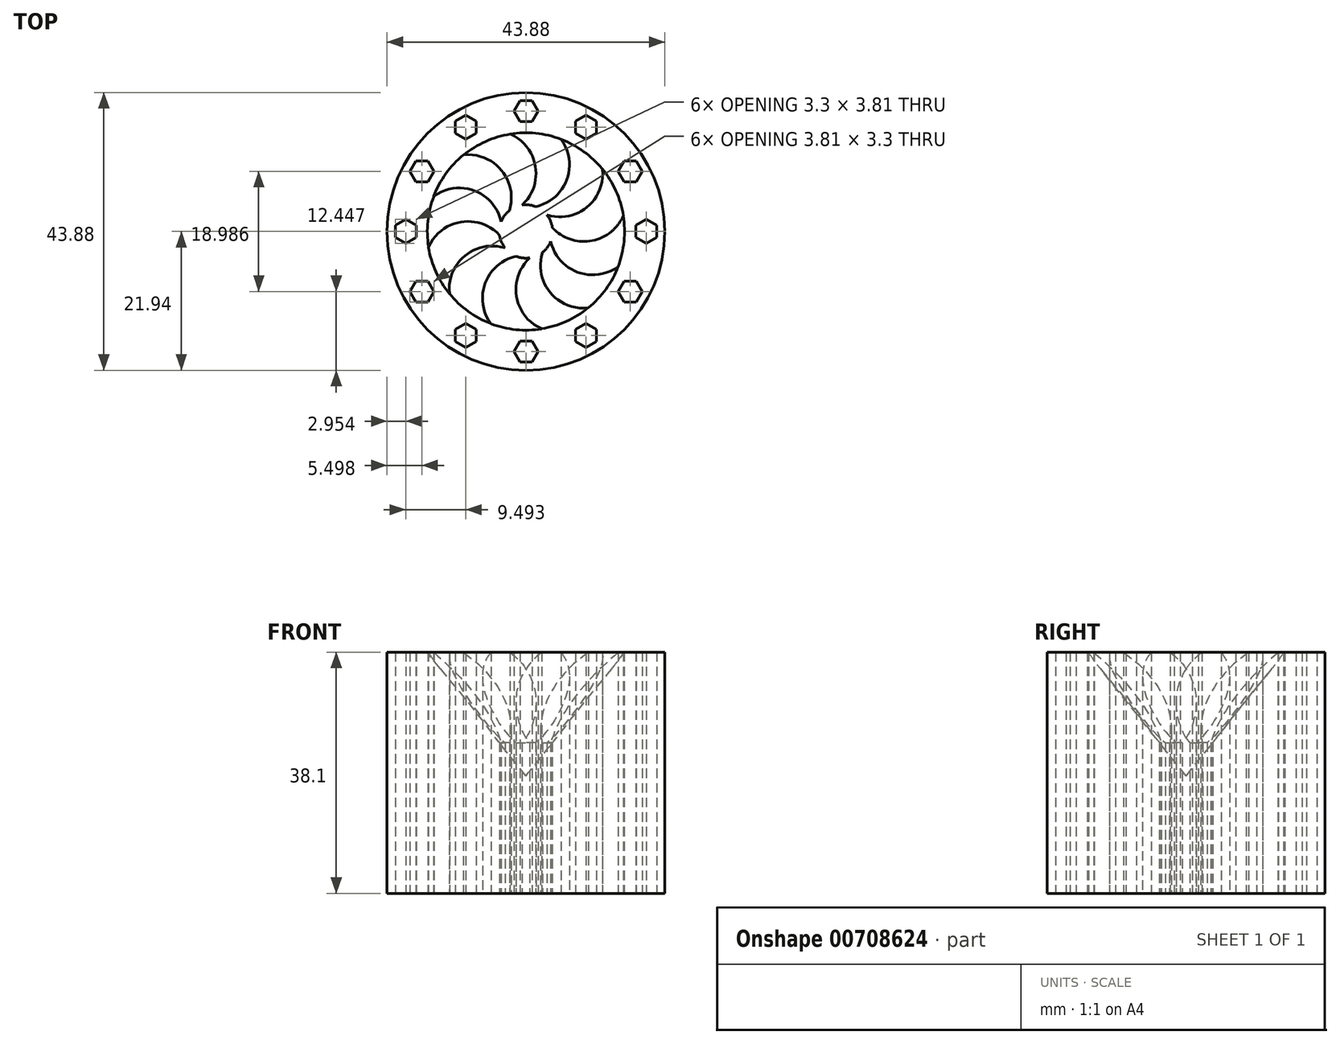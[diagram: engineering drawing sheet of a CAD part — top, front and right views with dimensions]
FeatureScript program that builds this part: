
annotation { "Feature Type Name" : "Feature", "Feature Type Description" : "" }
export const myFeature = defineFeature(function(context is Context, id is Id, definition is map)
    precondition{}
    {
        {
            var Q0;
            Q0=qCreatedBy(makeId("Top.planeOp"),FACE);
            var sketch = newSketch(context, id + "F0", { "sketchPlane" : qUnion([Q0])});
            skCircle(sketch, "E0", {"center": v(0, 0) * mm, "radius": 21.94 * mm});
            skCircle(sketch, "E1.0", {"center": v(0, 0) * mm, "radius": 15.59 * mm});
            skCircle(sketch, "E2.cCircle", {"center": v(0, 18.99) * mm, "radius": 1.65 * mm, "construction": true});
            skLineSegment(sketch, "E2.0", {"start": v(0.95, 17.34) * mm, "end": v(-0.95, 17.34) * mm});
            skLineSegment(sketch, "E2.1", {"start": v(-0.95, 17.34) * mm, "end": v(-1.9, 18.99) * mm});
            skLineSegment(sketch, "E2.2", {"start": v(-1.9, 18.99) * mm, "end": v(-0.95, 20.64) * mm});
            skLineSegment(sketch, "E2.3", {"start": v(-0.95, 20.64) * mm, "end": v(0.95, 20.64) * mm});
            skLineSegment(sketch, "E2.4", {"start": v(0.95, 20.64) * mm, "end": v(1.9, 18.99) * mm});
            skLineSegment(sketch, "E2.5", {"start": v(1.9, 18.99) * mm, "end": v(0.95, 17.34) * mm});
            skPoint(sketch, "E2.0.midPoint", {"position": v(0, 17.34) * mm});
            skLineSegment(sketch, "E3.1.0", {"start": v(-11.14, 15.5) * mm, "end": v(-11.14, 17.4) * mm});
            skLineSegment(sketch, "E3.1.1", {"start": v(-11.14, 17.4) * mm, "end": v(-9.5, 18.35) * mm});
            skLineSegment(sketch, "E3.1.2", {"start": v(-9.5, 18.35) * mm, "end": v(-7.84, 17.4) * mm});
            skLineSegment(sketch, "E3.1.3", {"start": v(-7.84, 17.4) * mm, "end": v(-7.84, 15.5) * mm});
            skLineSegment(sketch, "E3.1.4", {"start": v(-7.84, 15.5) * mm, "end": v(-9.5, 14.54) * mm});
            skLineSegment(sketch, "E3.1.5", {"start": v(-9.5, 14.54) * mm, "end": v(-11.14, 15.5) * mm});
            skLineSegment(sketch, "E3.2.0", {"start": v(-17.4, 7.84) * mm, "end": v(-18.35, 9.5) * mm});
            skLineSegment(sketch, "E3.2.1", {"start": v(-18.35, 9.5) * mm, "end": v(-17.4, 11.14) * mm});
            skLineSegment(sketch, "E3.2.2", {"start": v(-17.4, 11.14) * mm, "end": v(-15.5, 11.14) * mm});
            skLineSegment(sketch, "E3.2.3", {"start": v(-15.5, 11.14) * mm, "end": v(-14.54, 9.5) * mm});
            skLineSegment(sketch, "E3.2.4", {"start": v(-14.54, 9.5) * mm, "end": v(-15.5, 7.84) * mm});
            skLineSegment(sketch, "E3.2.5", {"start": v(-15.5, 7.84) * mm, "end": v(-17.4, 7.84) * mm});
            skLineSegment(sketch, "E3.3.0", {"start": v(-18.99, -1.9) * mm, "end": v(-20.64, -0.95) * mm});
            skLineSegment(sketch, "E3.3.1", {"start": v(-20.64, -0.95) * mm, "end": v(-20.64, 0.95) * mm});
            skLineSegment(sketch, "E3.3.2", {"start": v(-20.64, 0.95) * mm, "end": v(-18.99, 1.9) * mm});
            skLineSegment(sketch, "E3.3.3", {"start": v(-18.99, 1.9) * mm, "end": v(-17.34, 0.95) * mm});
            skLineSegment(sketch, "E3.3.4", {"start": v(-17.34, 0.95) * mm, "end": v(-17.34, -0.95) * mm});
            skLineSegment(sketch, "E3.3.5", {"start": v(-17.34, -0.95) * mm, "end": v(-18.99, -1.9) * mm});
            skLineSegment(sketch, "E3.4.0", {"start": v(-15.5, -11.14) * mm, "end": v(-17.4, -11.14) * mm});
            skLineSegment(sketch, "E3.4.1", {"start": v(-17.4, -11.14) * mm, "end": v(-18.35, -9.5) * mm});
            skLineSegment(sketch, "E3.4.2", {"start": v(-18.35, -9.5) * mm, "end": v(-17.4, -7.84) * mm});
            skLineSegment(sketch, "E3.4.3", {"start": v(-17.4, -7.84) * mm, "end": v(-15.5, -7.84) * mm});
            skLineSegment(sketch, "E3.4.4", {"start": v(-15.5, -7.84) * mm, "end": v(-14.54, -9.5) * mm});
            skLineSegment(sketch, "E3.4.5", {"start": v(-14.54, -9.5) * mm, "end": v(-15.5, -11.14) * mm});
            skLineSegment(sketch, "E3.5.0", {"start": v(-7.84, -17.4) * mm, "end": v(-9.5, -18.35) * mm});
            skLineSegment(sketch, "E3.5.1", {"start": v(-9.5, -18.35) * mm, "end": v(-11.14, -17.4) * mm});
            skLineSegment(sketch, "E3.5.2", {"start": v(-11.14, -17.4) * mm, "end": v(-11.14, -15.5) * mm});
            skLineSegment(sketch, "E3.5.3", {"start": v(-11.14, -15.5) * mm, "end": v(-9.5, -14.54) * mm});
            skLineSegment(sketch, "E3.5.4", {"start": v(-9.5, -14.54) * mm, "end": v(-7.84, -15.5) * mm});
            skLineSegment(sketch, "E3.5.5", {"start": v(-7.84, -15.5) * mm, "end": v(-7.84, -17.4) * mm});
            skLineSegment(sketch, "E3.6.0", {"start": v(1.9, -18.99) * mm, "end": v(0.95, -20.64) * mm});
            skLineSegment(sketch, "E3.6.1", {"start": v(0.95, -20.64) * mm, "end": v(-0.95, -20.64) * mm});
            skLineSegment(sketch, "E3.6.2", {"start": v(-0.95, -20.64) * mm, "end": v(-1.9, -18.99) * mm});
            skLineSegment(sketch, "E3.6.3", {"start": v(-1.9, -18.99) * mm, "end": v(-0.95, -17.34) * mm});
            skLineSegment(sketch, "E3.6.4", {"start": v(-0.95, -17.34) * mm, "end": v(0.95, -17.34) * mm});
            skLineSegment(sketch, "E3.6.5", {"start": v(0.95, -17.34) * mm, "end": v(1.9, -18.99) * mm});
            skLineSegment(sketch, "E3.7.0", {"start": v(11.14, -15.5) * mm, "end": v(11.14, -17.4) * mm});
            skLineSegment(sketch, "E3.7.1", {"start": v(11.14, -17.4) * mm, "end": v(9.5, -18.35) * mm});
            skLineSegment(sketch, "E3.7.2", {"start": v(9.5, -18.35) * mm, "end": v(7.84, -17.4) * mm});
            skLineSegment(sketch, "E3.7.3", {"start": v(7.84, -17.4) * mm, "end": v(7.84, -15.5) * mm});
            skLineSegment(sketch, "E3.7.4", {"start": v(7.84, -15.5) * mm, "end": v(9.5, -14.54) * mm});
            skLineSegment(sketch, "E3.7.5", {"start": v(9.5, -14.54) * mm, "end": v(11.14, -15.5) * mm});
            skLineSegment(sketch, "E3.8.0", {"start": v(17.4, -7.84) * mm, "end": v(18.35, -9.5) * mm});
            skLineSegment(sketch, "E3.8.1", {"start": v(18.35, -9.5) * mm, "end": v(17.4, -11.14) * mm});
            skLineSegment(sketch, "E3.8.2", {"start": v(17.4, -11.14) * mm, "end": v(15.5, -11.14) * mm});
            skLineSegment(sketch, "E3.8.3", {"start": v(15.5, -11.14) * mm, "end": v(14.54, -9.5) * mm});
            skLineSegment(sketch, "E3.8.4", {"start": v(14.54, -9.5) * mm, "end": v(15.5, -7.84) * mm});
            skLineSegment(sketch, "E3.8.5", {"start": v(15.5, -7.84) * mm, "end": v(17.4, -7.84) * mm});
            skLineSegment(sketch, "E3.9.0", {"start": v(18.99, 1.9) * mm, "end": v(20.64, 0.95) * mm});
            skLineSegment(sketch, "E3.9.1", {"start": v(20.64, 0.95) * mm, "end": v(20.64, -0.95) * mm});
            skLineSegment(sketch, "E3.9.2", {"start": v(20.64, -0.95) * mm, "end": v(18.99, -1.9) * mm});
            skLineSegment(sketch, "E3.9.3", {"start": v(18.99, -1.9) * mm, "end": v(17.34, -0.95) * mm});
            skLineSegment(sketch, "E3.9.4", {"start": v(17.34, -0.95) * mm, "end": v(17.34, 0.95) * mm});
            skLineSegment(sketch, "E3.9.5", {"start": v(17.34, 0.95) * mm, "end": v(18.99, 1.9) * mm});
            skLineSegment(sketch, "E3.10.0", {"start": v(15.5, 11.14) * mm, "end": v(17.4, 11.14) * mm});
            skLineSegment(sketch, "E3.10.1", {"start": v(17.4, 11.14) * mm, "end": v(18.35, 9.5) * mm});
            skLineSegment(sketch, "E3.10.2", {"start": v(18.35, 9.5) * mm, "end": v(17.4, 7.84) * mm});
            skLineSegment(sketch, "E3.10.3", {"start": v(17.4, 7.84) * mm, "end": v(15.5, 7.84) * mm});
            skLineSegment(sketch, "E3.10.4", {"start": v(15.5, 7.84) * mm, "end": v(14.54, 9.5) * mm});
            skLineSegment(sketch, "E3.10.5", {"start": v(14.54, 9.5) * mm, "end": v(15.5, 11.14) * mm});
            skLineSegment(sketch, "E3.11.0", {"start": v(7.84, 17.4) * mm, "end": v(9.5, 18.35) * mm});
            skLineSegment(sketch, "E3.11.1", {"start": v(9.5, 18.35) * mm, "end": v(11.14, 17.4) * mm});
            skLineSegment(sketch, "E3.11.2", {"start": v(11.14, 17.4) * mm, "end": v(11.14, 15.5) * mm});
            skLineSegment(sketch, "E3.11.3", {"start": v(11.14, 15.5) * mm, "end": v(9.5, 14.54) * mm});
            skLineSegment(sketch, "E3.11.4", {"start": v(9.5, 14.54) * mm, "end": v(7.84, 15.5) * mm});
            skLineSegment(sketch, "E3.11.5", {"start": v(7.84, 15.5) * mm, "end": v(7.84, 17.4) * mm});
            skCircle(sketch, "E4", {"center": v(0, 0) * mm, "radius": 4.21 * mm});
            skArc(sketch, "E5", {"start": v(-2.61, 3.3) * mm, "mid": v(-3.85, 9.66) * mm, "end": v(-9.86, 12.07) * mm});
            skArc(sketch, "E6.1.0", {"start": v(-0.61, 4.17) * mm, "mid": v(1.5, 10.3) * mm, "end": v(-2.5, 15.39) * mm});
            skArc(sketch, "E6.2.0", {"start": v(1.56, 3.92) * mm, "mid": v(6.44, 8.17) * mm, "end": v(5.52, 14.58) * mm});
            skArc(sketch, "E6.3.0", {"start": v(3.3, 2.61) * mm, "mid": v(9.66, 3.85) * mm, "end": v(12.07, 9.86) * mm});
            skArc(sketch, "E6.4.0", {"start": v(4.17, 0.61) * mm, "mid": v(10.3, -1.5) * mm, "end": v(15.39, 2.5) * mm});
            skArc(sketch, "E6.5.0", {"start": v(3.92, -1.56) * mm, "mid": v(8.17, -6.44) * mm, "end": v(14.58, -5.52) * mm});
            skArc(sketch, "E6.6.0", {"start": v(2.61, -3.3) * mm, "mid": v(3.85, -9.66) * mm, "end": v(9.86, -12.07) * mm});
            skArc(sketch, "E6.7.0", {"start": v(0.61, -4.17) * mm, "mid": v(-1.5, -10.3) * mm, "end": v(2.5, -15.39) * mm});
            skArc(sketch, "E6.8.0", {"start": v(-1.56, -3.92) * mm, "mid": v(-6.44, -8.17) * mm, "end": v(-5.52, -14.58) * mm});
            skArc(sketch, "E6.9.0", {"start": v(-3.3, -2.61) * mm, "mid": v(-9.66, -3.85) * mm, "end": v(-12.07, -9.86) * mm});
            skArc(sketch, "E6.10.0", {"start": v(-4.17, -0.61) * mm, "mid": v(-10.3, 1.5) * mm, "end": v(-15.39, -2.5) * mm});
            skArc(sketch, "E6.11.0", {"start": v(-3.92, 1.56) * mm, "mid": v(-8.17, 6.44) * mm, "end": v(-14.58, 5.52) * mm});
            skLineSegment(sketch, "E6.anchor1", {"start": v(0, 0) * mm, "end": v(-9.08, 5.34) * mm, "construction": true});
            skLineSegment(sketch, "E6.anchor2", {"start": v(0, 0) * mm, "end": v(-10.53, 0.09) * mm, "construction": true});
            skSolve(sketch);
        }
        {
            var Q0;
            {var subQ0=sQuery(id+"F0.wireOp",EDGE,"E5");Q0=makeQuery(id+"F0.imprint","IMPRINT",FACE,{"disambiguationData":[TD([[makeQuery(id+"F0.imprint","IMPRINT",EDGE,{"derivedFrom":subQ0}),-1.0]])]});}
            var Q1;
            {var subQ0=sQuery(id+"F0.wireOp",EDGE,"E6.2.0");Q1=makeQuery(id+"F0.imprint","IMPRINT",FACE,{"disambiguationData":[TD([[makeQuery(id+"F0.imprint","IMPRINT",EDGE,{"derivedFrom":subQ0}),-1.0]])]});}
            var Q2;
            {var subQ0=sQuery(id+"F0.wireOp",EDGE,"E6.4.0");Q2=makeQuery(id+"F0.imprint","IMPRINT",FACE,{"disambiguationData":[TD([[makeQuery(id+"F0.imprint","IMPRINT",EDGE,{"derivedFrom":subQ0}),-1.0]])]});}
            var Q3;
            {var subQ0=sQuery(id+"F0.wireOp",EDGE,"E6.6.0");Q3=makeQuery(id+"F0.imprint","IMPRINT",FACE,{"disambiguationData":[TD([[makeQuery(id+"F0.imprint","IMPRINT",EDGE,{"derivedFrom":subQ0}),-1.0]])]});}
            var Q4;
            {var subQ0=sQuery(id+"F0.wireOp",EDGE,"E6.8.0");Q4=makeQuery(id+"F0.imprint","IMPRINT",FACE,{"disambiguationData":[TD([[makeQuery(id+"F0.imprint","IMPRINT",EDGE,{"derivedFrom":subQ0}),-1.0]])]});}
            var Q5;
            {var subQ0=sQuery(id+"F0.wireOp",EDGE,"E6.10.0");Q5=makeQuery(id+"F0.imprint","IMPRINT",FACE,{"disambiguationData":[TD([[makeQuery(id+"F0.imprint","IMPRINT",EDGE,{"derivedFrom":subQ0}),-1.0]])]});}
            var Q6;
            Q6=makeQuery(id+"F0.imprint","IMPRINT",FACE,{"disambiguationData":[TD([[makeQuery(id+"F0.imprint","IMPRINT",EDGE,{"derivedFrom":sQuery(id+"F0.wireOp",EDGE,"E0")}),1.0]])]});
            var Q7;
            {var subQ0=sQuery(id+"F0.wireOp",EDGE,"E4");var subQ8=makeQuery(id+"F0.imprint","INTERSECT",VERTEX,{"derivedFrom":[subQ0,sQuery(id+"F0.wireOp",EDGE,"E6.3.0")]});Q7=makeQuery(id+"F0.imprint","IMPRINT",FACE,{"disambiguationData":[TD([[makeQuery(id+"F0.imprint","IMPRINT",EDGE,{"disambiguationData":[TD([[subQ8,1.0]])],"derivedFrom":subQ0}),1.0]])]});}
            extrude(context, id + "F1", {"entities" : qUnion([Q0, Q1, Q2, Q3, Q4, Q5, Q6, Q7]), "depth" : 38.1 * mm, "offsetDistance" : 25.4 * mm});
        }
        {
            var Q0;
            Q0=qCreatedBy(makeId("Right.planeOp"),FACE);
            var sketch = newSketch(context, id + "F2", { "sketchPlane" : qUnion([Q0])});
            skLineSegment(sketch, "E7", {"start": v(20.56, 54.38) * mm, "end": v(22.03, 53.28) * mm});
            skLineSegment(sketch, "E8", {"start": v(15.57, 38) * mm, "end": v(0, 18.54) * mm});
            skLineSegment(sketch, "E9", {"start": v(0, 18.54) * mm, "end": v(0, 39.07) * mm});
            skLineSegment(sketch, "E10", {"start": v(0, 39.07) * mm, "end": v(15.57, 39.07) * mm});
            skLineSegment(sketch, "E11", {"start": v(15.57, 39.07) * mm, "end": v(15.57, 38) * mm});
            skSolve(sketch);
        }
        {
            var Q0;
            Q0 = qSketchRegion(id + "F2", true);
            var Q1;
            Q1=sQuery(id+"F2.wireOp",EDGE,"E9");
            revolve(context, id + "F3", {"operationType" : NewBodyOperationType.REMOVE, "surfaceOperationType" : NewSurfaceOperationType.NEW, "entities" : qUnion([Q0]), "axis" : qUnion([Q1]), "revolveType" : RevolveType.FULL, "oppositeDirection" : true});
        }
    });
